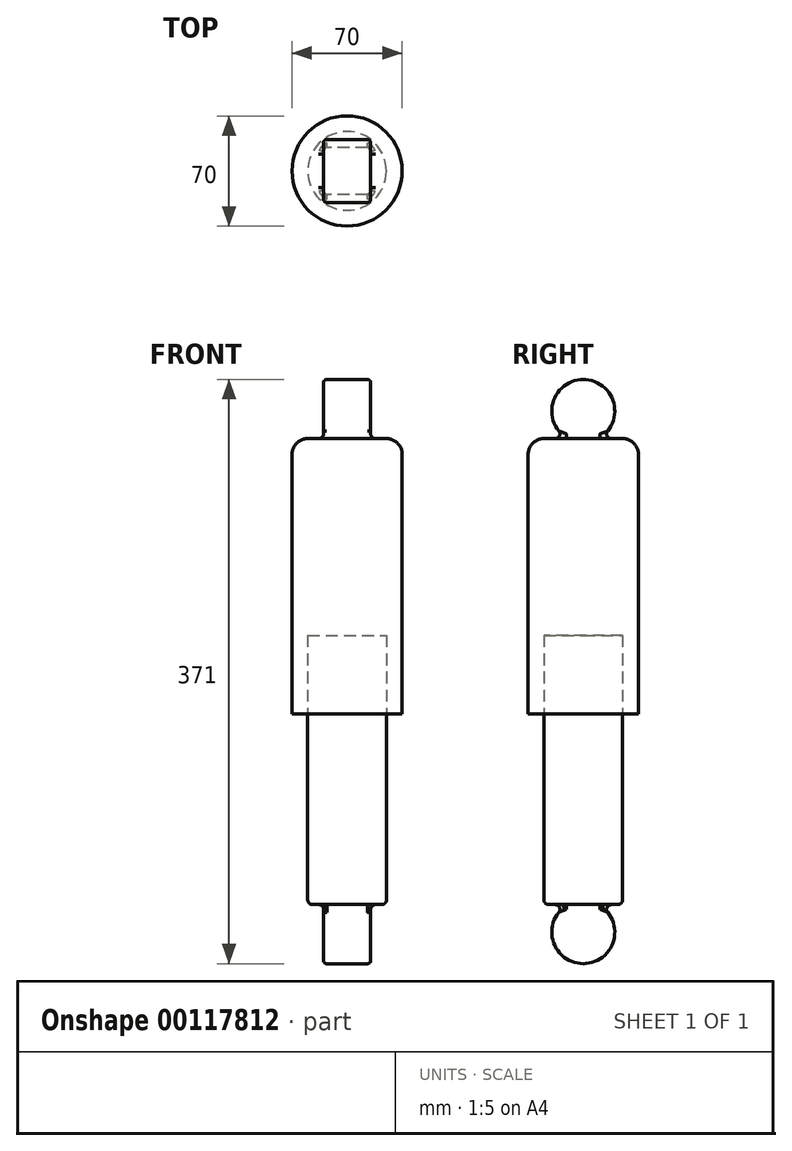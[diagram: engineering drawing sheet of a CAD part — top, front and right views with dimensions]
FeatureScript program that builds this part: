
annotation { "Feature Type Name" : "Feature", "Feature Type Description" : "" }
export const myFeature = defineFeature(function(context is Context, id is Id, definition is map)
    precondition{}
    {
        {
            var Q0;
            Q0=qCreatedBy(makeId("Right.planeOp"),FACE);
            var sketch = newSketch(context, id + "F0", { "sketchPlane" : qUnion([Q0])});
            skLineSegment(sketch, "E0", {"start": v(0, 0) * mm, "end": v(0, 331) * mm, "construction": true});
            skCircle(sketch, "E1", {"center": v(0, 0) * mm, "radius": 20 * mm});
            skCircle(sketch, "E2", {"center": v(0, 331) * mm, "radius": 20 * mm});
            skLineSegment(sketch, "E3.bottom", {"start": v(0, 313.5) * mm, "end": v(35, 313.5) * mm});
            skLineSegment(sketch, "E3.top", {"start": v(0, 138.5) * mm, "end": v(35, 138.5) * mm});
            skLineSegment(sketch, "E3.left", {"start": v(0, 313.5) * mm, "end": v(0, 138.5) * mm});
            skLineSegment(sketch, "E3.right", {"start": v(35, 313.5) * mm, "end": v(35, 138.5) * mm});
            skLineSegment(sketch, "E4.bottom", {"start": v(0, 17.5) * mm, "end": v(25, 17.5) * mm});
            skLineSegment(sketch, "E4.top", {"start": v(0, 188.5) * mm, "end": v(25, 188.5) * mm});
            skLineSegment(sketch, "E4.left", {"start": v(0, 17.5) * mm, "end": v(0, 188.5) * mm});
            skLineSegment(sketch, "E4.right", {"start": v(25, 17.5) * mm, "end": v(25, 188.5) * mm});
            skSolve(sketch);
        }
        {
            var Q0;
            {var subQ0=sQuery(id+"F0.wireOp",EDGE,"E3.bottom");var subQ1=sQuery(id+"F0.wireOp",EDGE,"E2");var subQ2=makeQuery(id+"F0.imprint","INTERSECT",VERTEX,{"derivedFrom":[subQ1,subQ0]});Q0=makeQuery(id+"F0.imprint","IMPRINT",FACE,{"disambiguationData":[TD([[makeQuery(id+"F0.imprint","IMPRINT",EDGE,{"disambiguationData":[TD([[subQ2,-1.0]])],"derivedFrom":subQ1}),1.0]])]});}
            var Q1;
            {var subQ0=sQuery(id+"F0.wireOp",EDGE,"E4.bottom");var subQ1=sQuery(id+"F0.wireOp",EDGE,"E1");var subQ2=makeQuery(id+"F0.imprint","INTERSECT",VERTEX,{"derivedFrom":[subQ1,subQ0]});Q1=makeQuery(id+"F0.imprint","IMPRINT",FACE,{"disambiguationData":[TD([[makeQuery(id+"F0.imprint","IMPRINT",EDGE,{"disambiguationData":[TD([[subQ2,1.0]])],"derivedFrom":subQ1}),1.0]])]});}
            var Q2;
            {var subQ0=sQuery(id+"F0.wireOp",EDGE,"E3.bottom");var subQ1=sQuery(id+"F0.wireOp",EDGE,"E2");var subQ2=makeQuery(id+"F0.imprint","INTERSECT",VERTEX,{"derivedFrom":[subQ1,subQ0]});Q2=makeQuery(id+"F0.imprint","IMPRINT",FACE,{"disambiguationData":[TD([[makeQuery(id+"F0.imprint","IMPRINT",EDGE,{"disambiguationData":[TD([[subQ2,1.0]])],"derivedFrom":subQ1}),1.0]])]});}
            var Q3;
            {var subQ0=sQuery(id+"F0.wireOp",EDGE,"E4.bottom");var subQ1=sQuery(id+"F0.wireOp",EDGE,"E1");var subQ2=makeQuery(id+"F0.imprint","INTERSECT",VERTEX,{"derivedFrom":[subQ1,subQ0]});Q3=makeQuery(id+"F0.imprint","IMPRINT",FACE,{"disambiguationData":[TD([[makeQuery(id+"F0.imprint","IMPRINT",EDGE,{"disambiguationData":[TD([[subQ2,-1.0]])],"derivedFrom":subQ1}),1.0]])]});}
            extrude(context, id + "F1", {"entities" : qUnion([Q0, Q1, Q2, Q3]), "endBound" : BoundingType.SYMMETRIC, "depth" : 30 * mm});
        }
        {
            var Q0;
            Q0=makeQuery(id+"F1.opExtrude","SWEPT_FACE",FACE,{"disambiguationData":[OSD([sQuery(id+"F0.wireOp",EDGE,"E1")])]});
            var Q1;
            Q1=makeQuery(id+"F1.opExtrude","SWEPT_FACE",FACE,{"disambiguationData":[OSD([sQuery(id+"F0.wireOp",EDGE,"E2")])]});
            fillet(context, id + "F2", {"entities" : qUnion([Q0, Q1]), "radius" : 2 * mm, "tangentPropagation" : true, "allowEdgeOverflow" : false});
        }
        {
            var Q0;
            {var subQ6=sQuery(id+"F0.wireOp",EDGE,"E3.right");Q0=makeQuery(id+"F0.imprint","IMPRINT",FACE,{"disambiguationData":[TD([[makeQuery(id+"F0.imprint","IMPRINT",EDGE,{"derivedFrom":subQ6}),-1.0]])]});}
            var Q1;
            {var subQ5=sQuery(id+"F0.wireOp",EDGE,"E4.top");Q1=makeQuery(id+"F0.imprint","IMPRINT",FACE,{"disambiguationData":[TD([[makeQuery(id+"F0.imprint","IMPRINT",EDGE,{"derivedFrom":subQ5}),-1.0]])]});}
            var Q2;
            Q2=sQuery(id+"F0.wireOp",EDGE,"E3.left");
            revolve(context, id + "F3", {"operationType" : NewBodyOperationType.ADD, "entities" : qUnion([Q0, Q1]), "axis" : qUnion([Q2]), "revolveType" : RevolveType.FULL});
        }
        {
            var Q0;
            Q0=makeQuery(id+"F3.opRevolve","SWEPT_EDGE",EDGE,{"disambiguationData":[OSD([sQuery(id+"F0.wireOp",EDGE,"E3.bottom"),sQuery(id+"F0.wireOp",EDGE,"E3.right")])]});
            fillet(context, id + "F4", {"entities" : qUnion([Q0]), "radius" : 10 * mm, "tangentPropagation" : true, "allowEdgeOverflow" : false});
        }
        {
            var Q0;
            {var subQ3=sQuery(id+"F0.wireOp",EDGE,"E1");var subQ6=sQuery(id+"F0.wireOp",EDGE,"E4.bottom");var subQ8=makeQuery(id+"F0.imprint","INTERSECT",VERTEX,{"derivedFrom":[subQ3,subQ6]});Q0=makeQuery(id+"F0.imprint","IMPRINT",FACE,{"disambiguationData":[TD([[makeQuery(id+"F0.imprint","IMPRINT",EDGE,{"disambiguationData":[TD([[subQ8,-1.0]])],"derivedFrom":subQ3}),-1.0]])]});}
            var Q1;
            {var subQ5=sQuery(id+"F0.wireOp",EDGE,"E4.top");Q1=makeQuery(id+"F0.imprint","IMPRINT",FACE,{"disambiguationData":[TD([[makeQuery(id+"F0.imprint","IMPRINT",EDGE,{"derivedFrom":subQ5}),-1.0]])]});}
            var Q2;
            Q2=sQuery(id+"F0.wireOp",EDGE,"E4.left");
            revolve(context, id + "F5", {"entities" : qUnion([Q0, Q1]), "axis" : qUnion([Q2]), "revolveType" : RevolveType.FULL});
        }
        {
            var Q0;
            Q0=makeQuery(id+"F5.opRevolve","SWEPT_BODY",BODY,{"disambiguationData":[OSD([sQuery(id+"F0.wireOp",EDGE,"E1"),sQuery(id+"F0.wireOp",EDGE,"E4.bottom"),sQuery(id+"F0.wireOp",EDGE,"E4.top"),sQuery(id+"F0.wireOp",EDGE,"E4.left"),sQuery(id+"F0.wireOp",EDGE,"E4.right")])]});
            var Q1;
            Q1=makeQuery(id+"F1.opExtrude","SWEPT_BODY",BODY,{"disambiguationData":[OSD([sQuery(id+"F0.wireOp",EDGE,"E1")])]});
            booleanBodies(context, id + "F6", {"operationType" : BooleanOperationType.UNION, "tools" : qUnion([Q0, Q1])});
        }
        {
            var Q0;
            Q0=makeQuery(id+"F5.opRevolve","SWEPT_EDGE",EDGE,{"disambiguationData":[OSD([sQuery(id+"F0.wireOp",EDGE,"E4.bottom"),sQuery(id+"F0.wireOp",EDGE,"E4.right")])]});
            fillet(context, id + "F7", {"entities" : qUnion([Q0]), "radius" : 3 * mm, "tangentPropagation" : true, "allowEdgeOverflow" : false});
        }
        {
            var Q0;
            Q0=makeQuery(id+"F3.boolean.opBoolean","INTERSECT",EDGE,{"derivedFrom":[makeQuery(id+"F1.opExtrude","CAP_FACE",FACE,{"disambiguationData":[OSD([sQuery(id+"F0.wireOp",EDGE,"E2")])],"isStart":false}),makeQuery(id+"F3.opRevolve","SWEPT_FACE",FACE,{"disambiguationData":[OSD([sQuery(id+"F0.wireOp",EDGE,"E3.bottom")])]})]});
            fillet(context, id + "F8", {"entities" : qUnion([Q0]), "radius" : 3 * mm, "tangentPropagation" : true, "allowEdgeOverflow" : false});
        }
        {
            var Q0;
            Q0=makeQuery(id+"F6.opBoolean","INTERSECT",EDGE,{"derivedFrom":[makeQuery(id+"F1.opExtrude","CAP_FACE",FACE,{"disambiguationData":[OSD([sQuery(id+"F0.wireOp",EDGE,"E1")])],"isStart":false}),makeQuery(id+"F5.opRevolve","SWEPT_FACE",FACE,{"disambiguationData":[OSD([sQuery(id+"F0.wireOp",EDGE,"E4.bottom")])]})]});
            fillet(context, id + "F9", {"entities" : qUnion([Q0]), "radius" : 3 * mm, "tangentPropagation" : true, "allowEdgeOverflow" : false});
        }
    });
